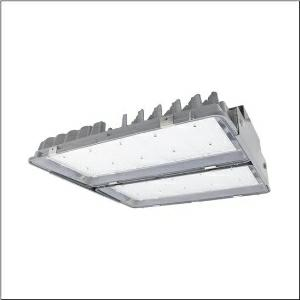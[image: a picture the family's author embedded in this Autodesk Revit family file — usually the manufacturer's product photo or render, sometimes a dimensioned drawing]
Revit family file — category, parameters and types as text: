
# Revit family: highbay_11xtreme_51hf81db4wma
name_source: partatom
category: Lighting Fixtures
units: mm (PartAtom-declared; Revit-internal decimal feet)

## family parameters
Cut with Voids When Loaded = No
Host = Face
Light Source = No
Part Type = Normal
Room Calculation Point = No
Round Connector Dimension = Use Diameter
Shared = No

## types (1)
- --- (1 x LED, 76000 lm, 422.2 W, 4000K)
    Apparent Load = 422 VA
    CIE Flux Codes = 88 96 99 100 100
    Color Rendering = 80
    Color Temperature = 4000K
    Default Elevation = 1800 mm
    Description = Highbay 11Xtreme, high bay luminaire, primary light control with lens, of PMMA, primary optical cover: cover, of toughened safety glass, light emission: direct distribution, primary light characteristic: symmetric, installation type: suspended mounting, surface-mounted, 2x LED module,for 1x 2x LED, rated luminous flux: 76.000lm, luminous efficacy: 180lm/W, light colour: 840, colour temperature: 4000K, control gear: DALI 2 (with two DALI addresses), with cable H07RN-F 5x 1.5mm², mains connection: 220..240V, AC, 50/60Hz, cable length: 1,5m, rated input power: 422W, luminaire housing, of diecast aluminium, partly coated, silver, length: 595mm, width: 560mm, height: 195mm, protection rating (complete): IP66, insulation class (complete): insulation class I (protective earthing), certification: CE, ENEC, UKCA, protection symbol: D, ball protection: ball impact resistant according to DIN VDE 0710 part 13 (with chain suspension), impact resistance: IK08, permissible operating ambient temperature: -25..+45°C, reducing of maximum allowable ambient temperature of 5°C with ceiling mounting, packaging unit: 1 piece
    Height = 157 mm
    Lamp = 1 x LED
    Lamp Light Flux = 76000 lm
    Lamp Power = 422.2 W
    Lamp count = 1
    Length = 593 mm
    Luminous efficacy = 180 lm/W
    Manufacturer = Siteco
    ModVariant = No
    Model = 51HF81DB4WMA
    Mounting Place = Ceiling
    Mounting Type = Pendant
    Number of Poles = 1
    OnlyDefault = Yes
    Power Factor = 1
    Product Name = Highbay 11Xtreme
    Product group = high bay luminaire
    ProductGroupID = 901
    Protection Class = Protection class I
    Protection Degree = IP 66
    RLX_Detail_Level = 1
    RLX_Emergency_Light_Flux = 0 lm
    RLX_Emergency_Type = 0
    RLX_Emergency_Type_DB = No
    RlxData = <blob elided: 33869 chars, md5=4464875c>
    Socket = socket
    Standby Power = 0 W
    System Light Flux = 76000 lm
    System Power = 422 W
    Type Comments = factory setting: luminous flux: 100 % | dim-lin: 254 | 1389 mA
    Type Image = l_1258340.jpg
    URL = http://relux.com
    VarID = @adj_083614
    Voltage = 0 V
    Weight = 0.00 kg
    Width = 278 mm

## geometry (parser evidence)
native form markers: Blend x4, Sweep x8
no freeform markers — native parametric forms only
